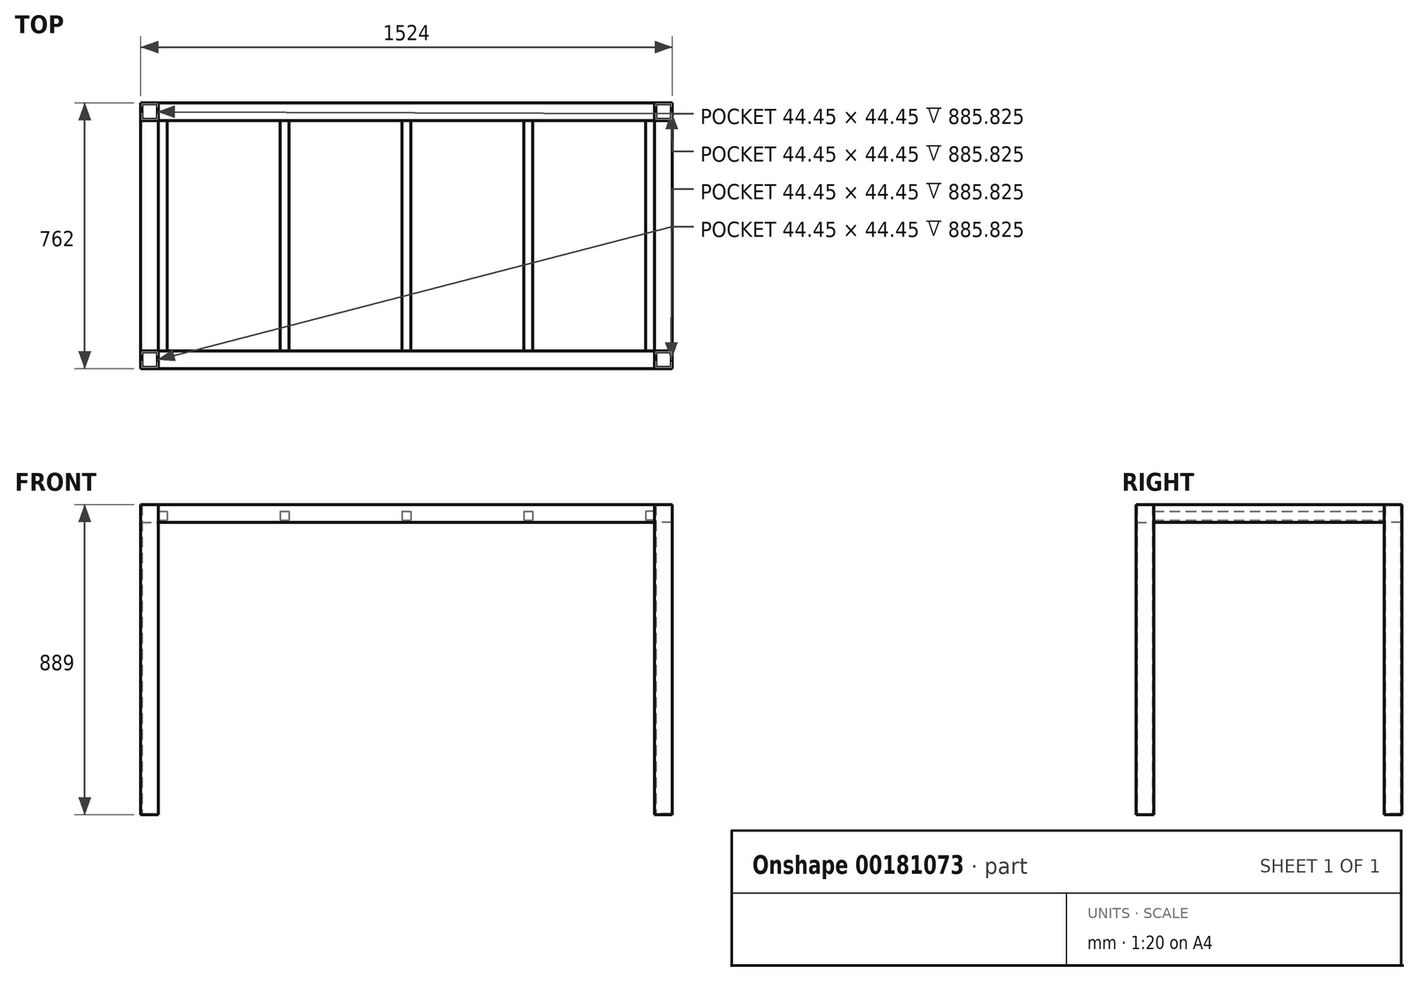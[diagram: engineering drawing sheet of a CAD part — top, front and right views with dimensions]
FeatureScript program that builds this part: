
annotation { "Feature Type Name" : "Feature", "Feature Type Description" : "" }
export const myFeature = defineFeature(function(context is Context, id is Id, definition is map)
    precondition{}
    {
        {
            var Q0;
            Q0=qCreatedBy(makeId("Top.planeOp"),FACE);
            var sketch = newSketch(context, id + "F0", { "sketchPlane" : qUnion([Q0])});
            skLineSegment(sketch, "E0.bottom", {"start": v(-762, 381) * mm, "end": v(-711.2, 381) * mm});
            skLineSegment(sketch, "E0.top", {"start": v(-762, 330.2) * mm, "end": v(-711.2, 330.2) * mm});
            skLineSegment(sketch, "E0.left", {"start": v(-762, 381) * mm, "end": v(-762, 330.2) * mm});
            skLineSegment(sketch, "E0.right", {"start": v(-711.2, 381) * mm, "end": v(-711.2, 330.2) * mm});
            skLineSegment(sketch, "E1.MirrorCS", {"start": v(762, 381) * mm, "end": v(762, 330.2) * mm});
            skLineSegment(sketch, "E2.MirrorCS", {"start": v(762, 381) * mm, "end": v(711.2, 381) * mm});
            skLineSegment(sketch, "E3.MirrorCS", {"start": v(711.2, 381) * mm, "end": v(711.2, 330.2) * mm});
            skLineSegment(sketch, "E4.MirrorCS", {"start": v(762, 330.2) * mm, "end": v(711.2, 330.2) * mm});
            skLineSegment(sketch, "E5.MirrorCS", {"start": v(762, -381) * mm, "end": v(762, -330.2) * mm});
            skLineSegment(sketch, "E6.MirrorCS", {"start": v(762, -330.2) * mm, "end": v(711.2, -330.2) * mm});
            skLineSegment(sketch, "E7.MirrorCS", {"start": v(711.2, -381) * mm, "end": v(711.2, -330.2) * mm});
            skLineSegment(sketch, "E8.MirrorCS", {"start": v(762, -381) * mm, "end": v(711.2, -381) * mm});
            skLineSegment(sketch, "E9.MirrorCS", {"start": v(-762, -381) * mm, "end": v(-711.2, -381) * mm});
            skLineSegment(sketch, "E10.MirrorCS", {"start": v(-762, -330.2) * mm, "end": v(-711.2, -330.2) * mm});
            skLineSegment(sketch, "E11.MirrorCS", {"start": v(-762, -381) * mm, "end": v(-762, -330.2) * mm});
            skLineSegment(sketch, "E12.MirrorCS", {"start": v(-711.2, -381) * mm, "end": v(-711.2, -330.2) * mm});
            skSolve(sketch);
        }
        {
            var Q0;
            Q0 = qSketchRegion(id + "F0", true);
            extrude(context, id + "F1", {"entities" : qUnion([Q0]), "depth" : 889 * mm});
        }
        {
            var Q0;
            Q0=makeQuery(id+"F1.opExtrude","CAP_FACE",FACE,{"disambiguationData":[OSD([sQuery(id+"F0.wireOp",EDGE,"E9.MirrorCS"),sQuery(id+"F0.wireOp",EDGE,"E10.MirrorCS"),sQuery(id+"F0.wireOp",EDGE,"E11.MirrorCS"),sQuery(id+"F0.wireOp",EDGE,"E12.MirrorCS")])],"isStart":false});
            var Q1;
            Q1=makeQuery(id+"F1.opExtrude","CAP_FACE",FACE,{"disambiguationData":[OSD([sQuery(id+"F0.wireOp",EDGE,"E0.bottom"),sQuery(id+"F0.wireOp",EDGE,"E0.top"),sQuery(id+"F0.wireOp",EDGE,"E0.left"),sQuery(id+"F0.wireOp",EDGE,"E0.right")])],"isStart":false});
            var Q2;
            Q2=makeQuery(id+"F1.opExtrude","CAP_FACE",FACE,{"disambiguationData":[OSD([sQuery(id+"F0.wireOp",EDGE,"E1.MirrorCS"),sQuery(id+"F0.wireOp",EDGE,"E2.MirrorCS"),sQuery(id+"F0.wireOp",EDGE,"E4.MirrorCS"),sQuery(id+"F0.wireOp",EDGE,"E3.MirrorCS")])],"isStart":false});
            var Q3;
            Q3=makeQuery(id+"F1.opExtrude","CAP_FACE",FACE,{"disambiguationData":[OSD([sQuery(id+"F0.wireOp",EDGE,"E7.MirrorCS"),sQuery(id+"F0.wireOp",EDGE,"E6.MirrorCS"),sQuery(id+"F0.wireOp",EDGE,"E8.MirrorCS"),sQuery(id+"F0.wireOp",EDGE,"E5.MirrorCS")])],"isStart":false});
            var Q4;
            Q4=makeQuery(id+"F1.opExtrude","SWEPT_BODY",BODY,{"disambiguationData":[OSD([sQuery(id+"F0.wireOp",EDGE,"E9.MirrorCS"),sQuery(id+"F0.wireOp",EDGE,"E10.MirrorCS"),sQuery(id+"F0.wireOp",EDGE,"E11.MirrorCS"),sQuery(id+"F0.wireOp",EDGE,"E12.MirrorCS")])]});
            var Q5;
            Q5=makeQuery(id+"F1.opExtrude","SWEPT_BODY",BODY,{"disambiguationData":[OSD([sQuery(id+"F0.wireOp",EDGE,"E0.bottom"),sQuery(id+"F0.wireOp",EDGE,"E0.top"),sQuery(id+"F0.wireOp",EDGE,"E0.left"),sQuery(id+"F0.wireOp",EDGE,"E0.right")])]});
            var Q6;
            Q6=makeQuery(id+"F1.opExtrude","SWEPT_BODY",BODY,{"disambiguationData":[OSD([sQuery(id+"F0.wireOp",EDGE,"E1.MirrorCS"),sQuery(id+"F0.wireOp",EDGE,"E2.MirrorCS"),sQuery(id+"F0.wireOp",EDGE,"E4.MirrorCS"),sQuery(id+"F0.wireOp",EDGE,"E3.MirrorCS")])]});
            var Q7;
            Q7=makeQuery(id+"F1.opExtrude","SWEPT_BODY",BODY,{"disambiguationData":[OSD([sQuery(id+"F0.wireOp",EDGE,"E7.MirrorCS"),sQuery(id+"F0.wireOp",EDGE,"E6.MirrorCS"),sQuery(id+"F0.wireOp",EDGE,"E8.MirrorCS"),sQuery(id+"F0.wireOp",EDGE,"E5.MirrorCS")])]});
            shell(context, id + "F2", {"entities" : qUnion([Q0, Q1, Q2, Q3]), "parts" : qUnion([Q4, Q5, Q6, Q7]), "thickness" : 3.17 * mm});
        }
        {
            var Q0;
            Q0=makeQuery(id+"F1.opExtrude","SWEPT_FACE",FACE,{"disambiguationData":[OSD([sQuery(id+"F0.wireOp",EDGE,"E0.top")])]});
            var sketch = newSketch(context, id + "F3", { "sketchPlane" : qUnion([Q0])});
            skLineSegment(sketch, "E13.bottom", {"start": v(-762, 889) * mm, "end": v(-711.2, 889) * mm});
            skLineSegment(sketch, "E13.top", {"start": v(-762, 838.2) * mm, "end": v(-711.2, 838.2) * mm});
            skLineSegment(sketch, "E13.left", {"start": v(-762, 889) * mm, "end": v(-762, 838.2) * mm});
            skLineSegment(sketch, "E13.right", {"start": v(-711.2, 889) * mm, "end": v(-711.2, 838.2) * mm});
            skLineSegment(sketch, "E14.MirrorCS", {"start": v(711.2, 889) * mm, "end": v(711.2, 838.2) * mm});
            skLineSegment(sketch, "E15.MirrorCS", {"start": v(762, 889) * mm, "end": v(711.2, 889) * mm});
            skLineSegment(sketch, "E16.MirrorCS", {"start": v(762, 889) * mm, "end": v(762, 838.2) * mm});
            skLineSegment(sketch, "E17.MirrorCS", {"start": v(762, 838.2) * mm, "end": v(711.2, 838.2) * mm});
            skSolve(sketch);
        }
        {
            var Q0;
            Q0 = qSketchRegion(id + "F3", true);
            extrude(context, id + "F4", {"entities" : qUnion([Q0]), "depth" : 660.4 * mm});
        }
        {
            var Q0;
            Q0=makeQuery(id+"F1.opExtrude","SWEPT_FACE",FACE,{"disambiguationData":[OSD([sQuery(id+"F0.wireOp",EDGE,"E3.MirrorCS")])]});
            var sketch = newSketch(context, id + "F5", { "sketchPlane" : qUnion([Q0])});
            skLineSegment(sketch, "E18.bottom", {"start": v(-381, 889) * mm, "end": v(-330.2, 889) * mm});
            skLineSegment(sketch, "E18.top", {"start": v(-381, 838.2) * mm, "end": v(-330.2, 838.2) * mm});
            skLineSegment(sketch, "E18.left", {"start": v(-381, 889) * mm, "end": v(-381, 838.2) * mm});
            skLineSegment(sketch, "E18.right", {"start": v(-330.2, 889) * mm, "end": v(-330.2, 838.2) * mm});
            skLineSegment(sketch, "E19.MirrorCS", {"start": v(381, 889) * mm, "end": v(330.2, 889) * mm});
            skLineSegment(sketch, "E20.MirrorCS", {"start": v(381, 838.2) * mm, "end": v(330.2, 838.2) * mm});
            skLineSegment(sketch, "E21.MirrorCS", {"start": v(381, 889) * mm, "end": v(381, 838.2) * mm});
            skLineSegment(sketch, "E22.MirrorCS", {"start": v(330.2, 889) * mm, "end": v(330.2, 838.2) * mm});
            skSolve(sketch);
        }
        {
            var Q0;
            Q0 = qSketchRegion(id + "F5", true);
            extrude(context, id + "F6", {"entities" : qUnion([Q0]), "depth" : 1422.4 * mm});
        }
        {
            var Q0;
            Q0=makeQuery(id+"F6.opExtrude","SWEPT_FACE",FACE,{"disambiguationData":[OSD([sQuery(id+"F5.wireOp",EDGE,"E18.right")])]});
            var sketch = newSketch(context, id + "F7", { "sketchPlane" : qUnion([Q0])});
            skLineSegment(sketch, "E23.bottom", {"start": v(-361.95, 869.95) * mm, "end": v(-336.55, 869.95) * mm});
            skLineSegment(sketch, "E23.top", {"start": v(-361.95, 844.55) * mm, "end": v(-336.55, 844.55) * mm});
            skLineSegment(sketch, "E23.left", {"start": v(-361.95, 869.95) * mm, "end": v(-361.95, 844.55) * mm});
            skLineSegment(sketch, "E23.right", {"start": v(-336.55, 869.95) * mm, "end": v(-336.55, 844.55) * mm});
            skLineSegment(sketch, "E24.1.0.0", {"start": v(-12.7, 844.55) * mm, "end": v(12.7, 844.55) * mm});
            skLineSegment(sketch, "E24.1.0.1", {"start": v(-12.7, 869.95) * mm, "end": v(-12.7, 844.55) * mm});
            skLineSegment(sketch, "E24.1.0.2", {"start": v(12.7, 869.95) * mm, "end": v(12.7, 844.55) * mm});
            skLineSegment(sketch, "E24.1.0.3", {"start": v(-12.7, 869.95) * mm, "end": v(12.7, 869.95) * mm});
            skLineSegment(sketch, "E24.2.0.0", {"start": v(336.55, 844.55) * mm, "end": v(361.95, 844.55) * mm});
            skLineSegment(sketch, "E24.2.0.1", {"start": v(336.55, 869.95) * mm, "end": v(336.55, 844.55) * mm});
            skLineSegment(sketch, "E24.2.0.2", {"start": v(361.95, 869.95) * mm, "end": v(361.95, 844.55) * mm});
            skLineSegment(sketch, "E24.2.0.3", {"start": v(336.55, 869.95) * mm, "end": v(361.95, 869.95) * mm});
            skLineSegment(sketch, "E25.bottom", {"start": v(-711.2, 869.95) * mm, "end": v(-685.8, 869.95) * mm});
            skLineSegment(sketch, "E25.top", {"start": v(-711.2, 844.55) * mm, "end": v(-685.8, 844.55) * mm});
            skLineSegment(sketch, "E25.left", {"start": v(-711.2, 869.95) * mm, "end": v(-711.2, 844.55) * mm});
            skLineSegment(sketch, "E25.right", {"start": v(-685.8, 869.95) * mm, "end": v(-685.8, 844.55) * mm});
            skLineSegment(sketch, "E26.bottom", {"start": v(711.2, 869.95) * mm, "end": v(685.8, 869.95) * mm});
            skLineSegment(sketch, "E26.top", {"start": v(711.2, 844.55) * mm, "end": v(685.8, 844.55) * mm});
            skLineSegment(sketch, "E26.left", {"start": v(711.2, 869.95) * mm, "end": v(711.2, 844.55) * mm});
            skLineSegment(sketch, "E26.right", {"start": v(685.8, 869.95) * mm, "end": v(685.8, 844.55) * mm});
            skSolve(sketch);
        }
        {
            var Q0;
            Q0 = qSketchRegion(id + "F7", true);
            extrude(context, id + "F8", {"entities" : qUnion([Q0]), "depth" : 660.4 * mm});
        }
    });
